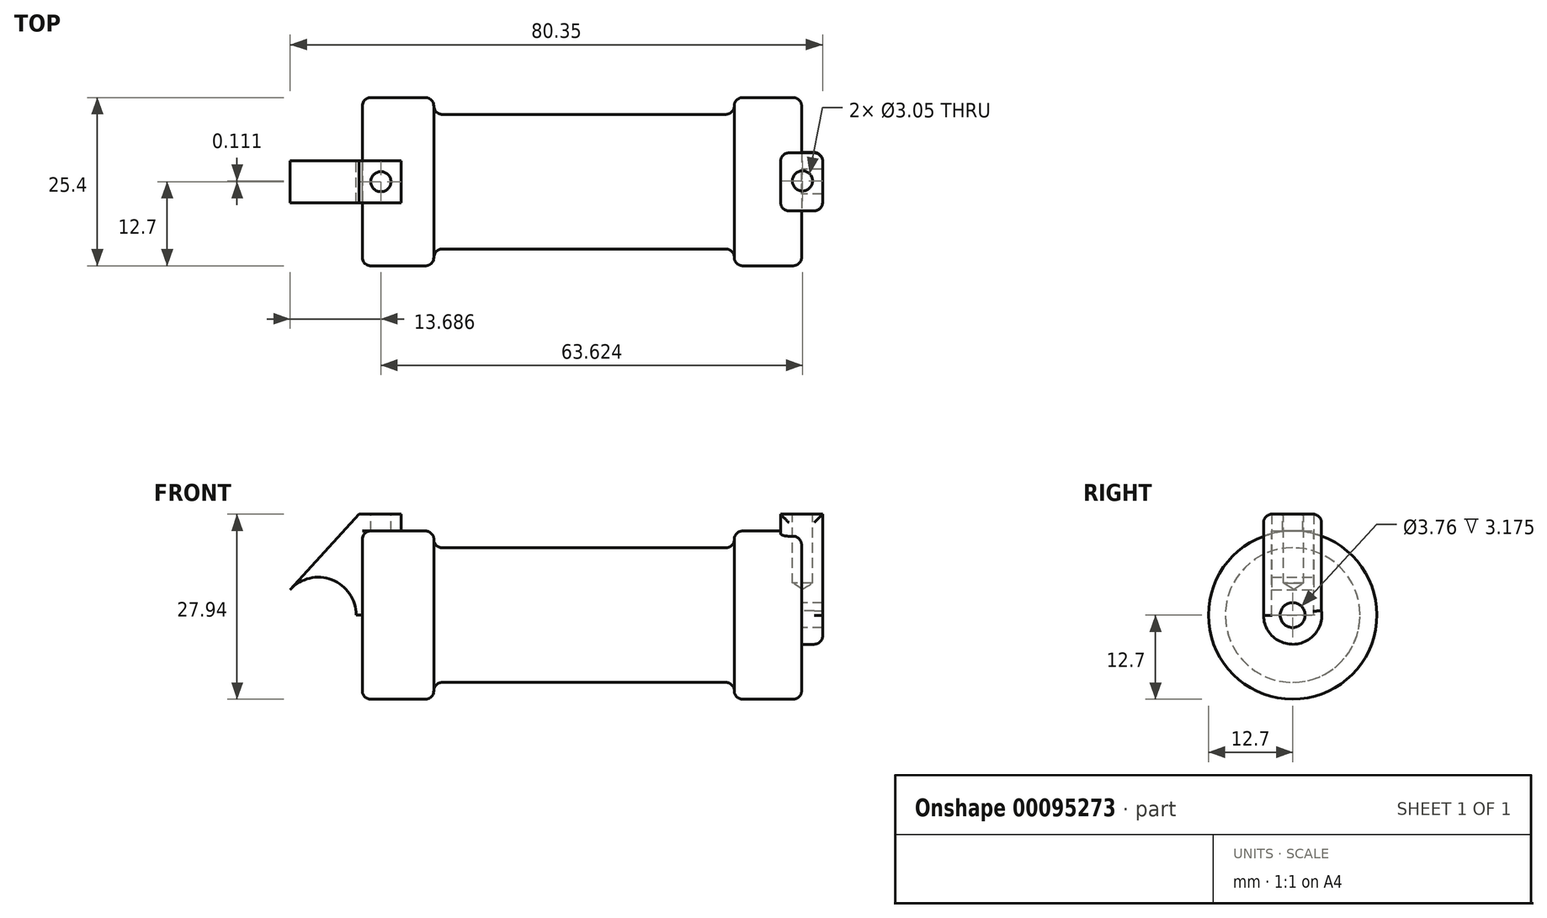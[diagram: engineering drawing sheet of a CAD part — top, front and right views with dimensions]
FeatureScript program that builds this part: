
annotation { "Feature Type Name" : "Feature", "Feature Type Description" : "" }
export const myFeature = defineFeature(function(context is Context, id is Id, definition is map)
    precondition{}
    {
        {
            var Q0;
            Q0=qCreatedBy(makeId("Front.planeOp"),FACE);
            var sketch = newSketch(context, id + "F0", { "sketchPlane" : qUnion([Q0])});
            skLineSegment(sketch, "E0", {"start": v(0, 0) * mm, "end": v(0, 12.7) * mm});
            skLineSegment(sketch, "E1", {"start": v(0, 12.7) * mm, "end": v(10.16, 12.7) * mm});
            skLineSegment(sketch, "E2", {"start": v(10.16, 12.7) * mm, "end": v(10.16, 10.16) * mm});
            skLineSegment(sketch, "E3", {"start": v(10.16, 10.16) * mm, "end": v(56.13, 10.16) * mm});
            skLineSegment(sketch, "E4", {"start": v(56.13, 10.16) * mm, "end": v(56.13, 12.7) * mm});
            skLineSegment(sketch, "E5", {"start": v(56.13, 12.7) * mm, "end": v(66.3, 12.7) * mm});
            skLineSegment(sketch, "E6", {"start": v(66.3, 12.7) * mm, "end": v(66.3, 0) * mm});
            skLineSegment(sketch, "E7", {"start": v(66.3, 0) * mm, "end": v(0, 0) * mm});
            skLineSegment(sketch, "E8", {"start": v(5.84, 15.24) * mm, "end": v(-0.5, 15.24) * mm});
            skLineSegment(sketch, "E9", {"start": v(-0.5, 15.24) * mm, "end": v(-10.88, 3.85) * mm});
            skLineSegment(sketch, "E10", {"start": v(0, 0) * mm, "end": v(-6.65, 0) * mm});
            skCircle(sketch, "E11", {"center": v(-6.65, 0) * mm, "radius": 5.72 * mm});
            skCircle(sketch, "E12", {"center": v(-6.65, 0) * mm, "radius": 3.18 * mm});
            skLineSegment(sketch, "E13", {"start": v(5.84, 15.24) * mm, "end": v(5.84, -10.16) * mm});
            skLineSegment(sketch, "E14", {"start": v(5.84, -10.16) * mm, "end": v(-8.45, -5.43) * mm});
            skPoint(sketch, "E15", {"position": v(0.06, -8.24) * mm});
            skPoint(sketch, "E16", {"position": v(-8.45, -5.43) * mm});
            skSolve(sketch);
        }
        {
            var Q0;
            {var subQ0=sQuery(id+"F0.wireOp",EDGE,"E2");Q0=makeQuery(id+"F0.imprint","IMPRINT",FACE,{"disambiguationData":[TD([[makeQuery(id+"F0.imprint","IMPRINT",EDGE,{"derivedFrom":subQ0}),-1.0]])]});}
            var Q1;
            {var subQ0=sQuery(id+"F0.wireOp",EDGE,"E0");Q1=makeQuery(id+"F0.imprint","IMPRINT",FACE,{"disambiguationData":[TD([[makeQuery(id+"F0.imprint","IMPRINT",EDGE,{"derivedFrom":subQ0}),-1.0]])]});}
            var Q2;
            Q2=sQuery(id+"F0.wireOp",EDGE,"E7");
            revolve(context, id + "F1", {"entities" : qUnion([Q0, Q1]), "axis" : qUnion([Q2]), "revolveType" : RevolveType.FULL});
        }
        {
            var Q0;
            {var subQ3=sQuery(id+"F0.wireOp",EDGE,"E0");Q0=makeQuery(id+"F0.imprint","IMPRINT",FACE,{"disambiguationData":[TD([[makeQuery(id+"F0.imprint","IMPRINT",EDGE,{"derivedFrom":subQ3}),1.0]])]});}
            extrude(context, id + "F2", {"entities" : qUnion([Q0]), "endBound" : BoundingType.SYMMETRIC, "depth" : 6.35 * mm});
        }
        {
            var Q0;
            Q0=makeQuery(id+"F1.opRevolve","SWEPT_FACE",FACE,{"disambiguationData":[OSD([sQuery(id+"F0.wireOp",EDGE,"E2")])]});
            extrude(context, id + "F3", {"entities" : qUnion([Q0]), "operationType" : NewBodyOperationType.ADD, "endBound" : BoundingType.SYMMETRIC, "depth" : 1.27 * mm});
        }
        {
            var Q0;
            Q0=makeQuery(id+"F2.opExtrude","SWEPT_FACE",FACE,{"disambiguationData":[OSD([sQuery(id+"F0.wireOp",EDGE,"E8")])]});
            var sketch = newSketch(context, id + "F4", { "sketchPlane" : qUnion([Q0])});
            skPoint(sketch, "E17", {"position": v(2.8, 0) * mm});
            skPoint(sketch, "E17.positionSnap0", {"position": v(-0.5, 0) * mm});
            skSolve(sketch);
        }
        {
            var Q0;
            Q0=sQuery(id+"F4.wireOp",VERTEX,"E17");
            var Q1;
            Q1=makeQuery(id+"F2.opExtrude","SWEPT_BODY",BODY,{"disambiguationData":[OSD([sQuery(id+"F0.wireOp",EDGE,"E0"),sQuery(id+"F0.wireOp",EDGE,"E1"),sQuery(id+"F0.wireOp",EDGE,"E8"),sQuery(id+"F0.wireOp",EDGE,"E9"),sQuery(id+"F0.wireOp",EDGE,"E10"),sQuery(id+"F0.wireOp",EDGE,"E11"),sQuery(id+"F0.wireOp",EDGE,"E13")])]});
            hole(context, id + "F5", {"style" : HoleStyle.SIMPLE, "endStyle" : HoleEndStyle.BLIND, "holeDiameter" : 3.05 * mm, "holeDepth" : 17.78 * mm, "locations" : qUnion([Q0]), "scope" : qUnion([Q1])});
        }
        {
            var Q0;
            Q0=makeQuery(id+"F1.opRevolve","SWEPT_FACE",FACE,{"disambiguationData":[OSD([sQuery(id+"F0.wireOp",EDGE,"E6")])]});
            var sketch = newSketch(context, id + "F6", { "sketchPlane" : qUnion([Q0])});
            skCircle(sketch, "E18", {"center": v(0, 0) * mm, "radius": 1.88 * mm});
            skCircle(sketch, "E19", {"center": v(0, 0) * mm, "radius": 4.4 * mm});
            skLineSegment(sketch, "E20.bottom", {"start": v(-0.03, 15.24) * mm, "end": v(-4.4, 15.24) * mm});
            skLineSegment(sketch, "E20.right", {"start": v(-4.4, 15.24) * mm, "end": v(-4.4, -0.09) * mm});
            skLineSegment(sketch, "E21.MirrorCS", {"start": v(4.35, 15.24) * mm, "end": v(4.35, -0.09) * mm});
            skLineSegment(sketch, "E22.MirrorCS", {"start": v(-0.03, 15.24) * mm, "end": v(4.35, 15.24) * mm});
            skSolve(sketch);
        }
        {
            var Q0;
            {var subQ1=sQuery(id+"F6.wireOp",EDGE,"E20.bottom");Q0=makeQuery(id+"F6.imprint","IMPRINT",FACE,{"disambiguationData":[TD([[makeQuery(id+"F6.imprint","IMPRINT",EDGE,{"derivedFrom":subQ1}),1.0]])]});}
            var Q1;
            {var subQ0=sQuery(id+"F6.wireOp",EDGE,"E21.MirrorCS");var subQ1=sQuery(id+"F6.wireOp",EDGE,"E19");var subQ2=makeQuery(id+"F6.imprint","INTERSECT",VERTEX,{"derivedFrom":[subQ1,subQ0]});Q1=makeQuery(id+"F6.imprint","IMPRINT",FACE,{"disambiguationData":[TD([[makeQuery(id+"F6.imprint","IMPRINT",EDGE,{"disambiguationData":[TD([[subQ2,-1.0]])],"derivedFrom":subQ1}),-1.0]])]});}
            var Q2;
            Q2=makeQuery(id+"F6.imprint","IMPRINT",FACE,{"disambiguationData":[TD([[makeQuery(id+"F6.imprint","IMPRINT",EDGE,{"derivedFrom":sQuery(id+"F6.wireOp",EDGE,"E18")}),-1.0]])]});
            extrude(context, id + "F7", {"entities" : qUnion([Q0, Q1, Q2]), "operationType" : NewBodyOperationType.ADD, "endBound" : BoundingType.SYMMETRIC, "depth" : 6.35 * mm});
        }
        {
            var Q0;
            Q0=makeQuery(id+"F7.opExtrude","SWEPT_FACE",FACE,{"disambiguationData":[OSD([sQuery(id+"F6.wireOp",EDGE,"E20.bottom"),sQuery(id+"F6.wireOp",EDGE,"E22.MirrorCS")])]});
            var sketch = newSketch(context, id + "F8", { "sketchPlane" : qUnion([Q0])});
            skPoint(sketch, "E23", {"position": v(66.43, 0.11) * mm});
            skSolve(sketch);
        }
        {
            var Q0;
            Q0=sQuery(id+"F8.wireOp",VERTEX,"E23");
            var Q1;
            Q1=makeQuery(id+"F1.opRevolve","SWEPT_BODY",BODY,{"disambiguationData":[OSD([sQuery(id+"F0.wireOp",EDGE,"E1"),sQuery(id+"F0.wireOp",EDGE,"E2"),sQuery(id+"F0.wireOp",EDGE,"E3"),sQuery(id+"F0.wireOp",EDGE,"E4"),sQuery(id+"F0.wireOp",EDGE,"E5"),sQuery(id+"F0.wireOp",EDGE,"E6"),sQuery(id+"F0.wireOp",EDGE,"E7"),sQuery(id+"F0.wireOp",EDGE,"E13")])]});
            hole(context, id + "F9", {"style" : HoleStyle.SIMPLE, "endStyle" : HoleEndStyle.BLIND, "holeDiameter" : 3.05 * mm, "holeDepth" : 10.4 * mm, "startFromSketch" : true, "locations" : qUnion([Q0]), "scope" : qUnion([Q1])});
        }
        {
            var Q0;
            Q0=makeQuery(id+"F1.opRevolve","SWEPT_EDGE",EDGE,{"disambiguationData":[OSD([sQuery(id+"F0.wireOp",EDGE,"E4"),sQuery(id+"F0.wireOp",EDGE,"E5")])]});
            fillet(context, id + "F10", {"entities" : qUnion([Q0]), "radius" : 1.27 * mm, "tangentPropagation" : true, "allowEdgeOverflow" : false});
        }
        {
            var Q0;
            Q0=makeQuery(id+"F3.opExtrude","CAP_EDGE",EDGE,{"disambiguationData":[OSD([sQuery(id+"F0.wireOp",EDGE,"E1"),sQuery(id+"F0.wireOp",EDGE,"E2")])],"isStart":false});
            var Q1;
            Q1=makeQuery(id+"F05ki8IrOCovVp2_3.opRevolve","SWEPT_EDGE",EDGE,{"disambiguationData":[OSD([sQuery(id+"F0.wireOp",EDGE,"E0"),sQuery(id+"F0.wireOp",EDGE,"E1")])]});
            var Q2;
            Q2=makeQuery(id+"F7.opExtrude","SWEPT_EDGE",EDGE,{"disambiguationData":[OSD([sQuery(id+"F6.wireOp",EDGE,"E20.right"),sQuery(id+"F6.wireOp",EDGE,"E20.bottom")])]});
            var Q3;
            Q3=makeQuery(id+"F7.opExtrude","CAP_EDGE",EDGE,{"disambiguationData":[OSD([sQuery(id+"F6.wireOp",EDGE,"E20.right")])],"isStart":true});
            var Q4;
            Q4=makeQuery(id+"F1.opRevolve","SWEPT_FACE",FACE,{"disambiguationData":[OSD([sQuery(id+"F0.wireOp",EDGE,"E3")])]});
            var Q5;
            Q5=makeQuery(id+"F7.opExtrude","CAP_EDGE",EDGE,{"disambiguationData":[OSD([sQuery(id+"F6.wireOp",EDGE,"E20.right")])],"isStart":false});
            fillet(context, id + "F11", {"entities" : qUnion([Q0, Q1, Q2, Q3, Q4, Q5]), "radius" : 1.27 * mm, "tangentPropagation" : true, "allowEdgeOverflow" : false});
        }
        {
            var Q0;
            Q0=makeQuery(id+"F7.opExtrude","CAP_EDGE",EDGE,{"disambiguationData":[OSD([sQuery(id+"F6.wireOp",EDGE,"E21.MirrorCS")])],"isStart":false});
            var Q1;
            Q1=makeQuery(id+"F7.opExtrude","CAP_EDGE",EDGE,{"disambiguationData":[OSD([sQuery(id+"F6.wireOp",EDGE,"E19")])],"isStart":false});
            var Q2;
            Q2=makeQuery(id+"F7.opExtrude","SWEPT_EDGE",EDGE,{"disambiguationData":[OSD([sQuery(id+"F6.wireOp",EDGE,"E21.MirrorCS"),sQuery(id+"F6.wireOp",EDGE,"E22.MirrorCS")])]});
            var Q3;
            Q3=makeQuery(id+"F7.opExtrude","CAP_EDGE",EDGE,{"disambiguationData":[OSD([sQuery(id+"F6.wireOp",EDGE,"E21.MirrorCS")])],"isStart":true});
            var Q4;
            Q4=makeQuery(id+"F1.opRevolve","SWEPT_EDGE",EDGE,{"disambiguationData":[OSD([sQuery(id+"F0.wireOp",EDGE,"E5"),sQuery(id+"F0.wireOp",EDGE,"E6")])]});
            fillet(context, id + "F12", {"entities" : qUnion([Q0, Q1, Q2, Q3, Q4]), "radius" : 1.27 * mm, "tangentPropagation" : true, "allowEdgeOverflow" : false});
        }
        {
            var Q0;
            Q0=makeQuery(id+"F1.opRevolve","SWEPT_EDGE",EDGE,{"disambiguationData":[OSD([sQuery(id+"F0.wireOp",EDGE,"E0"),sQuery(id+"F0.wireOp",EDGE,"E1")])]});
            fillet(context, id + "F13", {"entities" : qUnion([Q0]), "radius" : 1.27 * mm, "tangentPropagation" : true, "allowEdgeOverflow" : false});
        }
    });
